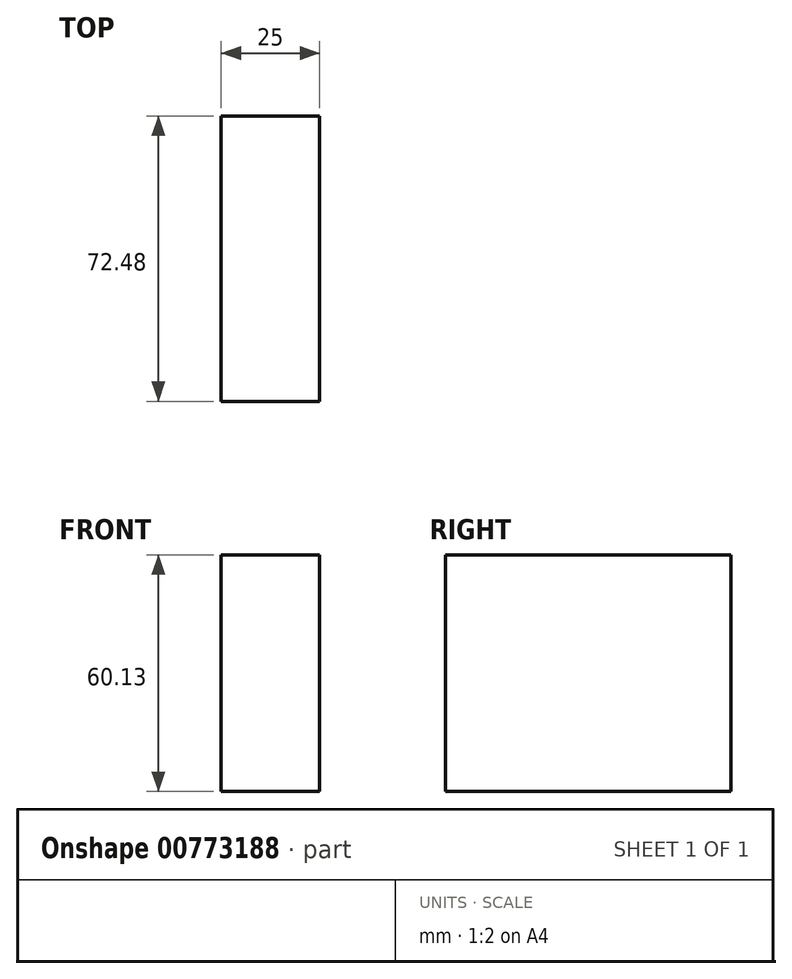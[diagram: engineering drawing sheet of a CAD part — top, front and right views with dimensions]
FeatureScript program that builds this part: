
annotation { "Feature Type Name" : "Feature", "Feature Type Description" : "" }
export const myFeature = defineFeature(function(context is Context, id is Id, definition is map)
    precondition{}
    {
        {
            var Q0;
            Q0=qCreatedBy(makeId("Right.planeOp"),FACE);
            var sketch = newSketch(context, id + "F0", { "sketchPlane" : qUnion([Q0])});
            skLineSegment(sketch, "E0.bottom", {"start": v(-29.57, -19.91) * mm, "end": v(42.9, -19.91) * mm});
            skLineSegment(sketch, "E0.top", {"start": v(-29.57, 40.22) * mm, "end": v(42.9, 40.22) * mm});
            skLineSegment(sketch, "E0.left", {"start": v(-29.57, -19.91) * mm, "end": v(-29.57, 40.22) * mm});
            skLineSegment(sketch, "E0.right", {"start": v(42.9, -19.91) * mm, "end": v(42.9, 40.22) * mm});
            skSolve(sketch);
        }
        {
            var Q0;
            Q0=makeQuery(id+"F0.imprint","IMPRINT",FACE,{"disambiguationData":[TD([[makeQuery(id+"F0.imprint","IMPRINT",EDGE,{"derivedFrom":sQuery(id+"F0.wireOp",EDGE,"E0.bottom")}),1.0]])]});
            extrude(context, id + "F1", {"entities" : qUnion([Q0]), "depth" : 25 * mm, "offsetDistance" : 25 * mm});
        }
    });
